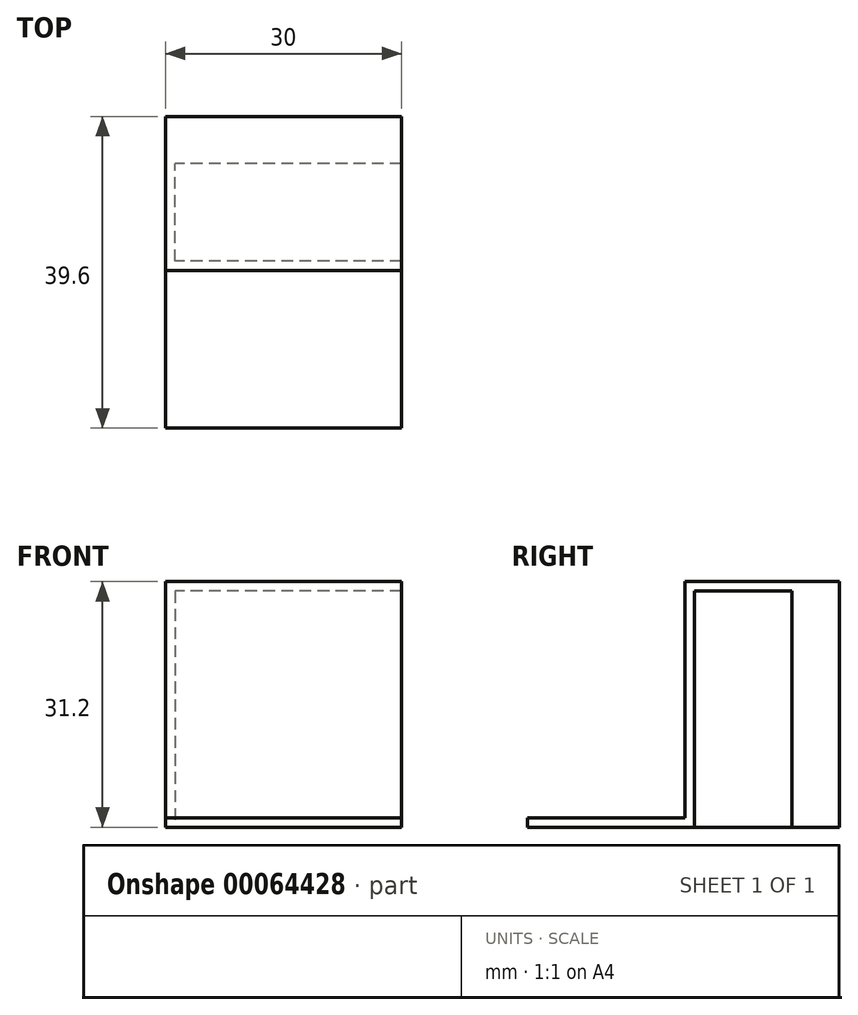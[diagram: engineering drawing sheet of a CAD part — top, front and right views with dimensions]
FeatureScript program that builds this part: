
annotation { "Feature Type Name" : "Feature", "Feature Type Description" : "" }
export const myFeature = defineFeature(function(context is Context, id is Id, definition is map)
    precondition{}
    {
        {
            var Q0;
            Q0=qCreatedBy(makeId("Top.planeOp"),FACE);
            var sketch = newSketch(context, id + "F0", { "sketchPlane" : qUnion([Q0])});
            skLineSegment(sketch, "E0.bottom", {"start": v(0, 0) * mm, "end": v(30, 0) * mm});
            skLineSegment(sketch, "E0.top", {"start": v(0, -21.2) * mm, "end": v(30, -21.2) * mm});
            skLineSegment(sketch, "E0.left", {"start": v(0, 0) * mm, "end": v(0, -21.2) * mm});
            skLineSegment(sketch, "E0.right", {"start": v(30, 0) * mm, "end": v(30, -21.2) * mm});
            skSolve(sketch);
        }
        {
            var Q0;
            Q0=makeQuery(id+"F0.imprint","IMPRINT",FACE,{"disambiguationData":[TD([[makeQuery(id+"F0.imprint","IMPRINT",EDGE,{"derivedFrom":sQuery(id+"F0.wireOp",EDGE,"E0.bottom")}),-1.0]])]});
            extrude(context, id + "F1", {"entities" : qUnion([Q0]), "depth" : 1.2 * mm});
        }
        {
            var Q0;
            Q0=makeQuery(id+"F1.opExtrude","CAP_FACE",FACE,{"disambiguationData":[OSD([sQuery(id+"F0.wireOp",EDGE,"E0.bottom"),sQuery(id+"F0.wireOp",EDGE,"E0.top"),sQuery(id+"F0.wireOp",EDGE,"E0.left"),sQuery(id+"F0.wireOp",EDGE,"E0.right")])],"isStart":false});
            var sketch = newSketch(context, id + "F2", { "sketchPlane" : qUnion([Q0])});
            skLineSegment(sketch, "E1", {"start": v(0, -1.2) * mm, "end": v(30, -1.2) * mm});
            skLineSegment(sketch, "E2", {"start": v(30, -1.2) * mm, "end": v(30, 0) * mm});
            skLineSegment(sketch, "E3", {"start": v(0, -1.2) * mm, "end": v(0, 0) * mm});
            skSolve(sketch);
        }
        {
            var Q0;
            Q0=makeQuery(id+"F2.imprint","IMPRINT",FACE,{"disambiguationData":[TD([[makeQuery(id+"F2.imprint","IMPRINT",EDGE,{"derivedFrom":sQuery(id+"F2.wireOp",EDGE,"E2")}),-1.0]])]});
            extrude(context, id + "F3", {"entities" : qUnion([Q0]), "operationType" : NewBodyOperationType.ADD, "depth" : 30 * mm});
        }
        {
            var Q0;
            {var subQ0=sQuery(id+"F0.wireOp",EDGE,"E0.bottom");Q0=makeQuery(id+"F3.boolean.opBoolean","MERGE",FACE,{"derivedFrom":[makeQuery(id+"F1.opExtrude","SWEPT_FACE",FACE,{"disambiguationData":[OSD([subQ0])]}),makeQuery(id+"F3.opExtrude","SWEPT_FACE",FACE,{"disambiguationData":[OSD([subQ0])]})]});}
            var sketch = newSketch(context, id + "F4", { "sketchPlane" : qUnion([Q0])});
            skLineSegment(sketch, "E4", {"start": v(-1.2, 31.2) * mm, "end": v(-1.2, 0) * mm});
            skLineSegment(sketch, "E5", {"start": v(-1.2, 0) * mm, "end": v(0, 0) * mm});
            skLineSegment(sketch, "E6", {"start": v(-1.2, 31.2) * mm, "end": v(0, 31.2) * mm});
            skSolve(sketch);
        }
        {
            var Q0;
            Q0=qSketchRegion(id+"F4",true);
            var Q1;
            Q1=makeQuery(id+"F4.imprint","IMPRINT",FACE,{"disambiguationData":[TD([[makeQuery(id+"F4.imprint","IMPRINT",EDGE,{"derivedFrom":sQuery(id+"F4.wireOp",EDGE,"E4")}),1.0]])]});
            extrude(context, id + "F5", {"entities" : qUnion([Q0, Q1]), "operationType" : NewBodyOperationType.ADD, "depth" : (10 + 1.2 + 6 + 1.2) * mm});
        }
        {
            var Q0;
            Q0=makeQuery(id+"F5.opExtrude","SWEPT_FACE",FACE,{"disambiguationData":[OSD([sQuery(id+"F4.wireOp",EDGE,"E4")])]});
            var sketch = newSketch(context, id + "F6", { "sketchPlane" : qUnion([Q0])});
            skLineSegment(sketch, "E7", {"start": v(12.4, 0) * mm, "end": v(12.4, 31.2) * mm});
            skLineSegment(sketch, "E8", {"start": v(12.4, 31.2) * mm, "end": v(18.4, 31.2) * mm});
            skLineSegment(sketch, "E9", {"start": v(12.4, 0) * mm, "end": v(18.4, 0) * mm});
            skSolve(sketch);
        }
        {
            var Q0;
            Q0=qSketchRegion(id+"F6",true);
            var Q1;
            Q1=makeQuery(id+"F6.imprint","IMPRINT",FACE,{"disambiguationData":[TD([[makeQuery(id+"F6.imprint","IMPRINT",EDGE,{"derivedFrom":sQuery(id+"F6.wireOp",EDGE,"E7")}),-1.0]])]});
            extrude(context, id + "F7", {"entities" : qUnion([Q0, Q1]), "operationType" : NewBodyOperationType.ADD, "depth" : (30 - 1.2) * mm});
        }
        {
            var Q0;
            Q0=makeQuery(id+"F7.opExtrude","SWEPT_FACE",FACE,{"disambiguationData":[OSD([sQuery(id+"F6.wireOp",EDGE,"E7")])]});
            var sketch = newSketch(context, id + "F8", { "sketchPlane" : qUnion([Q0])});
            skLineSegment(sketch, "E10", {"start": v(1.2, 30) * mm, "end": v(30, 30) * mm});
            skLineSegment(sketch, "E11", {"start": v(30, 30) * mm, "end": v(30, 31.2) * mm});
            skLineSegment(sketch, "E12", {"start": v(1.2, 30) * mm, "end": v(1.2, 31.2) * mm});
            skSolve(sketch);
        }
        {
            var Q0;
            Q0=makeQuery(id+"F8.imprint","IMPRINT",FACE,{"disambiguationData":[TD([[makeQuery(id+"F8.imprint","IMPRINT",EDGE,{"derivedFrom":sQuery(id+"F8.wireOp",EDGE,"E10")}),1.0]])]});
            extrude(context, id + "F9", {"entities" : qUnion([Q0]), "operationType" : NewBodyOperationType.ADD, "endBound" : BoundingType.UP_TO_NEXT, "depth" : 25 * mm});
        }
    });
